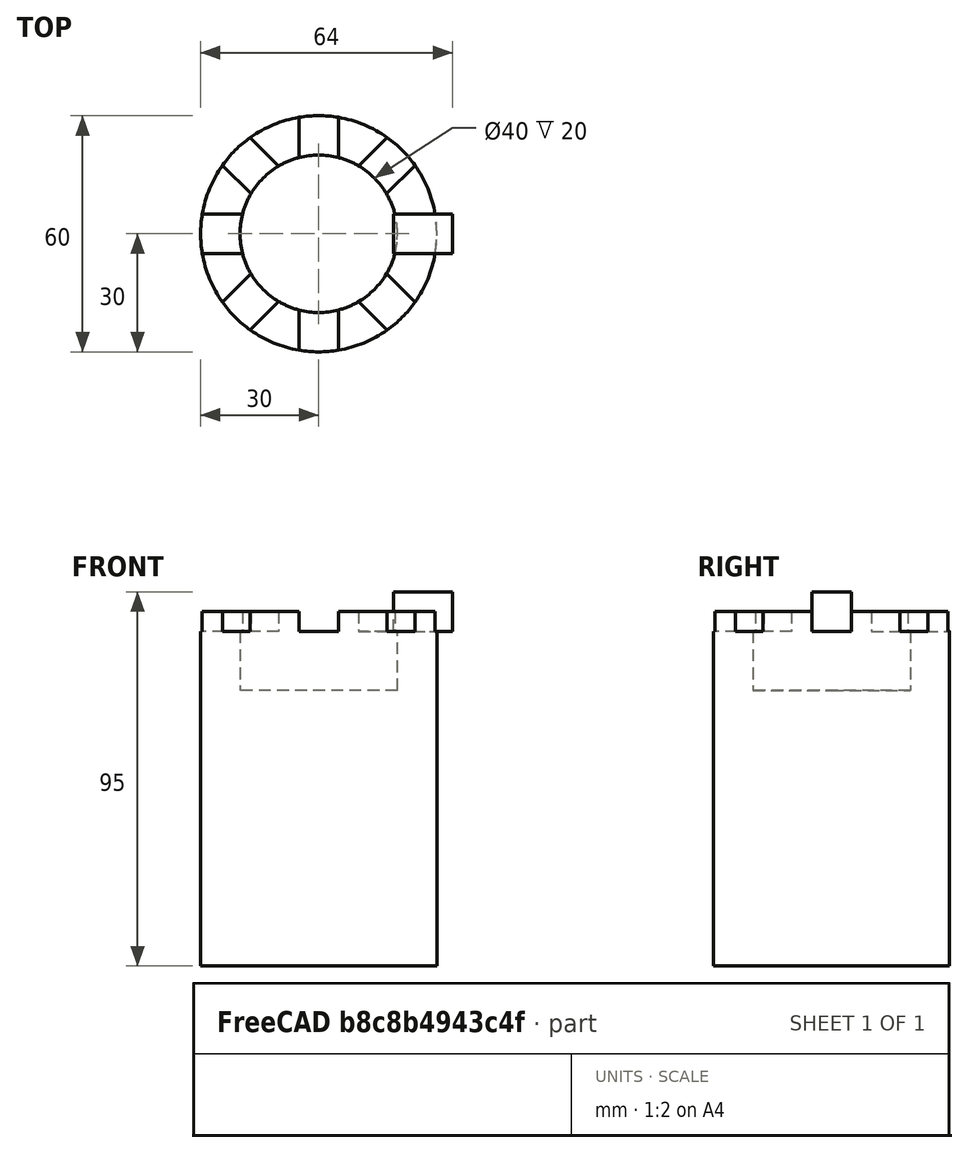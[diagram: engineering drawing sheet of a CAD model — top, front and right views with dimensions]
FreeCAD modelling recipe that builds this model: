
FCSTD DOCUMENT  (FreeCAD 0.21R33694 (Git))
Label: OJT1_T011R010_torre
License: All rights reserved
LicenseURL: http://en.wikipedia.org/wiki/All_rights_reserved
objects: Part::Cylinder×2, Part::Cut×2, Part::Box×1, Part::FeaturePython×1
note: 5 computed .brp shape members not serialized (recipe doc carries the construction recipe); baked Part::Feature solids carry a one-line shape summary decoded from their .brp

FEATURE [Part::Cylinder] Cylinder  label="torre"
  Angle = 360
  AttacherType = Attacher::AttachEngine3D
  FirstAngle = 0
  Height = 90
  Radius = 30
  SecondAngle = 0
FEATURE [Part::Cylinder] Cylinder001  label="part_de_dalt"
  Angle = 360
  AttacherType = Attacher::AttachEngine3D
  FirstAngle = 0
  Height = 20
  Placement = pos=(0,0,70) rot=(0,0,1;0rad)
  Radius = 20
  SecondAngle = 0
FEATURE [Part::Box] Box  label="talls_ranures"
  AttacherType = Attacher::AttachEngine3D
  Height = 10
  Length = 15
  Placement = pos=(19,-5,85) rot=(0,0,1;0rad)
  Width = 10
FEATURE [Part::Cut] Cut
  Base = -> Cylinder
  Refine = true
  Tool = -> Cylinder001
FEATURE [Part::FeaturePython] Array  # Draft array (typed FeaturePython)
  AlwaysSyncPlacement = false
  Angle = 360
  ArrayType = 1
  Axis = (0,0,1)
  Base = -> Box
  Center = (0,0,0)
  Count = 8
  ExpandArray = false
  Fuse = false
  IntervalAxis = (0,0,0)
  IntervalX = (50,0,0)
  IntervalY = (0,50,0)
  IntervalZ = (0,0,50)
  NumberCircles = 3
  NumberPolar = 8
  NumberX = 2
  NumberY = 2
  NumberZ = 1
  PlacementList = 8 placements: [(19,-5,85),(16.9706,9.89949,85),(5,19,85),(-9.89949,16.9706,85),(-19,5,85),(-16.9706,-9.89949,85),(-5,-19,85),(9.89949,-16.9706,85)]
  RadialDistance = 50
  ScaleList = (8) [(1,1,1),(1,1,1),(1,1,1),(1,1,1),(1,1,1),(1,1,1),(1,1,1),(1,1,1)]
  Symmetry = 1
  TangentialDistance = 25
FEATURE [Part::Cut] Cut001
  Base = -> Cut
  Refine = true
  Tool = -> Array
